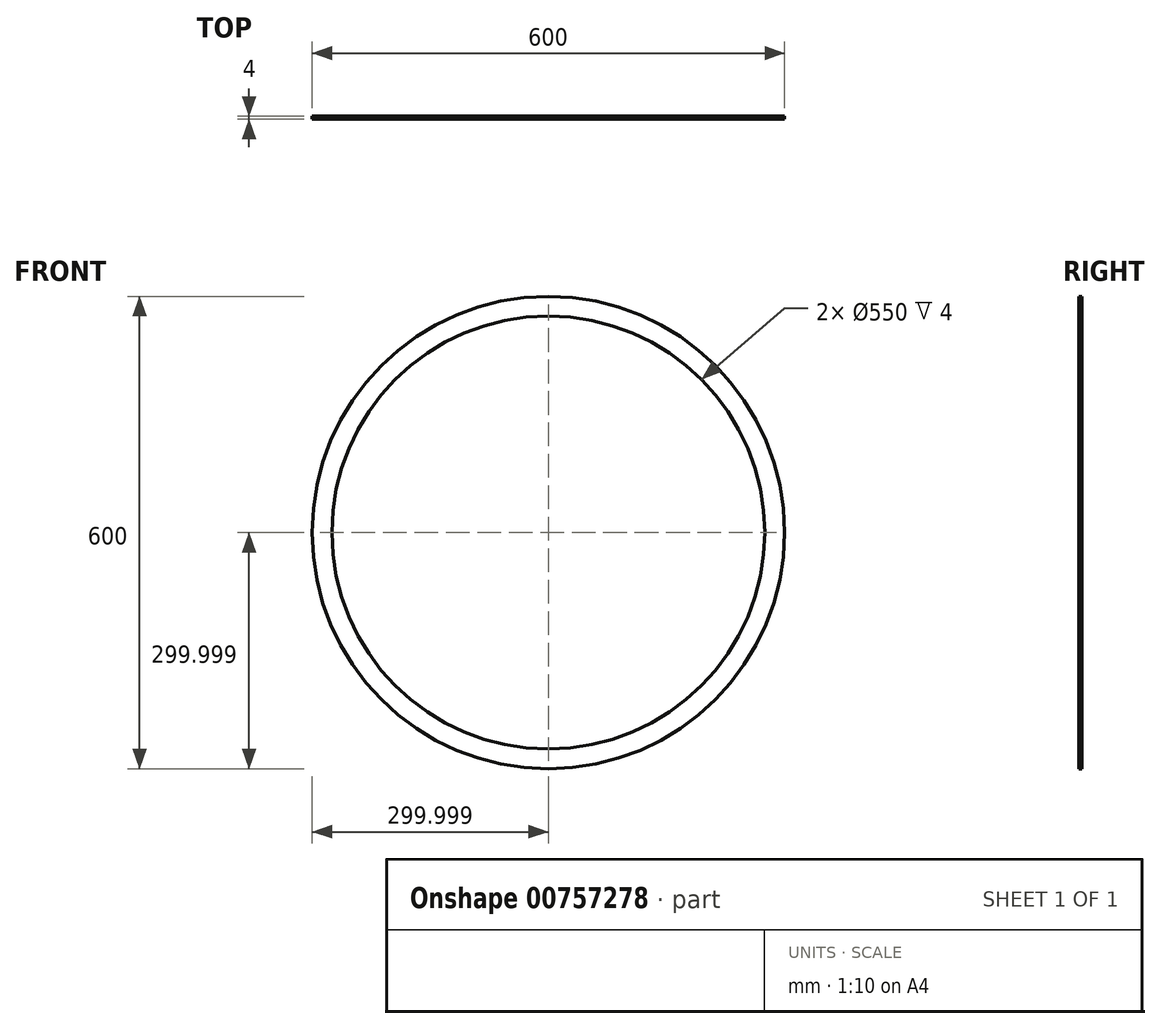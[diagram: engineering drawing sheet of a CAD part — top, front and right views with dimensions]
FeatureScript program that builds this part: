
annotation { "Feature Type Name" : "Feature", "Feature Type Description" : "" }
export const myFeature = defineFeature(function(context is Context, id is Id, definition is map)
    precondition{}
    {
        {
            var Q0;
            Q0=qCreatedBy(makeId("Front.planeOp"),FACE);
            var sketch = newSketch(context, id + "F0", { "sketchPlane" : qUnion([Q0])});
            skCircle(sketch, "E0", {"center": v(0.22, 0.22) * mm, "radius": 275 * mm});
            skCircle(sketch, "E1", {"center": v(0.22, 0.22) * mm, "radius": 300 * mm});
            skSolve(sketch);
        }
        {
            var Q0;
            Q0=makeQuery(id+"F0.imprint","IMPRINT",FACE,{"disambiguationData":[TD([[makeQuery(id+"F0.imprint","IMPRINT",EDGE,{"derivedFrom":sQuery(id+"F0.wireOp",EDGE,"E0")}),-1.0]])]});
            extrude(context, id + "F1", {"entities" : qUnion([Q0]), "depth" : 4 * mm, "offsetDistance" : 25 * mm});
        }
    });
